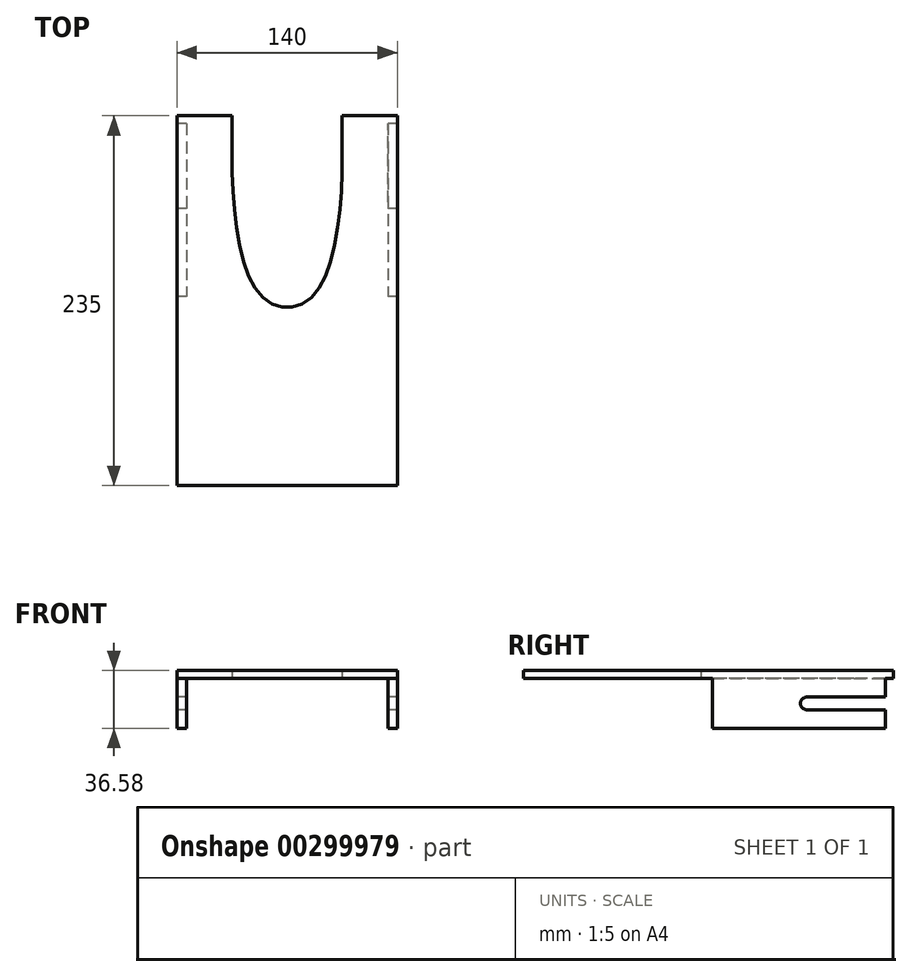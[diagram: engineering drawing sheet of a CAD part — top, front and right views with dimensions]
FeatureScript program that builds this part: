
annotation { "Feature Type Name" : "Feature", "Feature Type Description" : "" }
export const myFeature = defineFeature(function(context is Context, id is Id, definition is map)
    precondition{}
    {
        {
            var Q0;
            Q0=qCreatedBy(makeId("Top.planeOp"),FACE);
            var sketch = newSketch(context, id + "F0", { "sketchPlane" : qUnion([Q0])});
            skLineSegment(sketch, "E0.bottom", {"start": v(-66.5, 0) * mm, "end": v(73.5, 0) * mm});
            skLineSegment(sketch, "E0.top", {"start": v(-66.5, 110) * mm, "end": v(73.5, 110) * mm});
            skLineSegment(sketch, "E0.left", {"start": v(-66.5, 0) * mm, "end": v(-66.5, 110) * mm});
            skLineSegment(sketch, "E0.right", {"start": v(73.5, 0) * mm, "end": v(73.5, 110) * mm});
            skLineSegment(sketch, "E1", {"start": v(-66.5, 110) * mm, "end": v(-66.5, 210) * mm});
            skLineSegment(sketch, "E2", {"start": v(-66.5, 210) * mm, "end": v(-31.5, 210) * mm});
            skLineSegment(sketch, "E3", {"start": v(73.5, 110) * mm, "end": v(73.5, 210) * mm});
            skLineSegment(sketch, "E4", {"start": v(73.5, 210) * mm, "end": v(38.5, 210) * mm});
            skFitSpline(sketch, "E5", {"points": [v(-31.5, 210) * mm, v(-12.5, 120) * mm, v(19.5, 120) * mm, v(38.5, 210) * mm], "startDerivative": vector(0, -248.62) * mm, "endDerivative": vector(0, 248.62) * mm});
            skLineSegment(sketch, "E6.top", {"start": v(-66.5, 235) * mm, "end": v(-31.5, 235) * mm});
            skLineSegment(sketch, "E6.left", {"start": v(-66.5, 210) * mm, "end": v(-66.5, 235) * mm});
            skLineSegment(sketch, "E6.right", {"start": v(-31.5, 210) * mm, "end": v(-31.5, 235) * mm});
            skLineSegment(sketch, "E7.top", {"start": v(73.5, 235) * mm, "end": v(38.5, 235) * mm});
            skLineSegment(sketch, "E7.left", {"start": v(73.5, 210) * mm, "end": v(73.5, 235) * mm});
            skLineSegment(sketch, "E7.right", {"start": v(38.5, 210) * mm, "end": v(38.5, 235) * mm});
            skSolve(sketch);
        }
        {
            var Q0;
            Q0=qSketchRegion(id+"F0",true);
            extrude(context, id + "F1", {"entities" : qUnion([Q0]), "depth" : 4.83 * mm, "offsetDistance" : 25 * mm});
        }
        {
            var Q0;
            Q0=makeQuery(id+"F1.opExtrude","SWEPT_FACE",FACE,{"disambiguationData":[OSD([sQuery(id+"F0.wireOp",EDGE,"E0.bottom")])]});
            var sketch = newSketch(context, id + "F2", { "sketchPlane" : qUnion([Q0])});
            skLineSegment(sketch, "E8.bottom", {"start": v(-66.5, 0) * mm, "end": v(-34.75, 0) * mm});
            skLineSegment(sketch, "E8.top", {"start": v(-66.5, -31.75) * mm, "end": v(-34.75, -31.75) * mm});
            skLineSegment(sketch, "E8.left", {"start": v(-66.5, 0) * mm, "end": v(-66.5, -31.75) * mm});
            skLineSegment(sketch, "E8.right", {"start": v(-34.75, 0) * mm, "end": v(-34.75, -31.75) * mm});
            skLineSegment(sketch, "E9.bottom", {"start": v(73.5, 0) * mm, "end": v(41.75, 0) * mm});
            skLineSegment(sketch, "E9.top", {"start": v(73.5, -31.75) * mm, "end": v(41.75, -31.75) * mm});
            skLineSegment(sketch, "E9.left", {"start": v(73.5, 0) * mm, "end": v(73.5, -31.75) * mm});
            skLineSegment(sketch, "E9.right", {"start": v(41.75, 0) * mm, "end": v(41.75, -31.75) * mm});
            skLineSegment(sketch, "E10.bottom", {"start": v(-63.33, -3.17) * mm, "end": v(-37.93, -3.17) * mm});
            skLineSegment(sketch, "E10.top", {"start": v(-63.33, -28.57) * mm, "end": v(-37.93, -28.57) * mm});
            skLineSegment(sketch, "E10.left", {"start": v(-63.33, -3.17) * mm, "end": v(-63.33, -28.57) * mm});
            skLineSegment(sketch, "E10.right", {"start": v(-37.93, -3.17) * mm, "end": v(-37.93, -28.57) * mm});
            skLineSegment(sketch, "E11.bottom", {"start": v(44.92, -3.18) * mm, "end": v(70.33, -3.17) * mm});
            skLineSegment(sketch, "E11.top", {"start": v(44.92, -28.58) * mm, "end": v(70.33, -28.58) * mm});
            skLineSegment(sketch, "E11.left", {"start": v(44.92, -3.18) * mm, "end": v(44.92, -28.58) * mm});
            skLineSegment(sketch, "E11.right", {"start": v(70.33, -3.17) * mm, "end": v(70.33, -28.58) * mm});
            skSolve(sketch);
        }
        {
            var Q0;
            Q0=qSketchRegion(id+"F2",true);
            extrude(context, id + "F3", {"entities" : qUnion([Q0]), "operationType" : NewBodyOperationType.ADD, "oppositeDirection" : true, "depth" : 120 * mm});
        }
        {
            var Q0;
            Q0=makeQuery(id+"F3.opExtrude","CAP_FACE",FACE,{"disambiguationData":[OSD([sQuery(id+"F2.wireOp",EDGE,"E9.bottom"),sQuery(id+"F2.wireOp",EDGE,"E9.top"),sQuery(id+"F2.wireOp",EDGE,"E9.left"),sQuery(id+"F2.wireOp",EDGE,"E9.right"),sQuery(id+"F2.wireOp",EDGE,"E11.bottom"),sQuery(id+"F2.wireOp",EDGE,"E11.top"),sQuery(id+"F2.wireOp",EDGE,"E11.left"),sQuery(id+"F2.wireOp",EDGE,"E11.right")])],"isStart":false});
            var sketch = newSketch(context, id + "F4", { "sketchPlane" : qUnion([Q0])});
            skPoint(sketch, "E12.oppositeSnap0", {"position": v(-70.33, -15.88) * mm});
            skLineSegment(sketch, "E12.bottom", {"start": v(-73.5, 0) * mm, "end": v(-56, 0) * mm});
            skLineSegment(sketch, "E12.top", {"start": v(-73.5, -31.75) * mm, "end": v(-70.33, -31.75) * mm});
            skLineSegment(sketch, "E12.left", {"start": v(-73.5, 0) * mm, "end": v(-73.5, -31.75) * mm});
            skLineSegment(sketch, "E13.bottom", {"start": v(56, -31.75) * mm, "end": v(66.5, -31.75) * mm});
            skLineSegment(sketch, "E13.top", {"start": v(56, 0) * mm, "end": v(66.5, 0) * mm});
            skLineSegment(sketch, "E13.right", {"start": v(66.5, -31.75) * mm, "end": v(66.5, 0) * mm});
            skLineSegment(sketch, "E14", {"start": v(60.5, -31.75) * mm, "end": v(60.5, 0) * mm});
            skLineSegment(sketch, "E15", {"start": v(-67.5, 0) * mm, "end": v(-67.5, -31.75) * mm});
            skSolve(sketch);
        }
        {
            var Q0;
            Q0=qSketchRegion(id+"F4",true);
            var Q1;
            {var subQ5=makeQuery(id+"F3.opExtrude","CAP_EDGE",EDGE,{"disambiguationData":[OSD([sQuery(id+"F2.wireOp",EDGE,"E11.right")])],"isStart":false});Q1=makeQuery(id+"F4.imprint","IMPRINT",FACE,{"disambiguationData":[TD([[makeQuery(id+"F4.imprint","IMPRINT",EDGE,{"derivedFrom":subQ5}),1.0]])]});}
            var Q2;
            {var subQ6=sQuery(id+"F4.wireOp",EDGE,"E12.top");Q2=makeQuery(id+"F4.imprint","IMPRINT",FACE,{"disambiguationData":[TD([[makeQuery(id+"F4.imprint","IMPRINT",EDGE,{"derivedFrom":subQ6}),1.0]])]});}
            extrude(context, id + "F5", {"entities" : qUnion([Q0, Q1, Q2]), "operationType" : NewBodyOperationType.ADD, "depth" : 110 * mm, "offsetDistance" : 25 * mm});
        }
        {
            var Q0;
            {var subQ0=sQuery(id+"F2.wireOp",EDGE,"E8.right");Q0=makeQuery(id+"FrnK0tPHe9QpJH6_1.boolean.opBoolean","MERGE",FACE,{"derivedFrom":[makeQuery(id+"F3.opExtrude","SWEPT_FACE",FACE,{"disambiguationData":[OSD([subQ0])]}),makeQuery(id+"FrnK0tPHe9QpJH6_1.opExtrude","SWEPT_FACE",FACE,{"disambiguationData":[OSD([subQ0])]})]});}
            var sketch = newSketch(context, id + "F6", { "sketchPlane" : qUnion([Q0])});
            skCircle(sketch, "E16", {"center": v(60, -10) * mm, "radius": 3 * mm});
            skSolve(sketch);
        }
        {
            var Q0;
            Q0=qSketchRegion(id+"F6",true);
            extrude(context, id + "F7", {"entities" : qUnion([Q0]), "operationType" : NewBodyOperationType.REMOVE, "oppositeDirection" : true, "depth" : 10 * mm});
        }
        {
            var Q0;
            Q0=makeQuery(id+"F3.boolean.opBoolean","MERGE",FACE,{"derivedFrom":[makeQuery(id+"F1.opExtrude","SWEPT_FACE",FACE,{"disambiguationData":[OSD([sQuery(id+"F0.wireOp",EDGE,"E0.bottom")])]}),makeQuery(id+"F3.opExtrude","CAP_FACE",FACE,{"disambiguationData":[OSD([sQuery(id+"F2.wireOp",EDGE,"E8.bottom"),sQuery(id+"F2.wireOp",EDGE,"E8.top"),sQuery(id+"F2.wireOp",EDGE,"E8.left"),sQuery(id+"F2.wireOp",EDGE,"E8.right"),sQuery(id+"F2.wireOp",EDGE,"E10.bottom"),sQuery(id+"F2.wireOp",EDGE,"E10.top"),sQuery(id+"F2.wireOp",EDGE,"E10.left"),sQuery(id+"F2.wireOp",EDGE,"E10.right")])],"isStart":true}),makeQuery(id+"F3.opExtrude","CAP_FACE",FACE,{"disambiguationData":[OSD([sQuery(id+"F2.wireOp",EDGE,"E9.bottom"),sQuery(id+"F2.wireOp",EDGE,"E9.top"),sQuery(id+"F2.wireOp",EDGE,"E9.left"),sQuery(id+"F2.wireOp",EDGE,"E9.right"),sQuery(id+"F2.wireOp",EDGE,"E11.bottom"),sQuery(id+"F2.wireOp",EDGE,"E11.top"),sQuery(id+"F2.wireOp",EDGE,"E11.left"),sQuery(id+"F2.wireOp",EDGE,"E11.right")])],"isStart":true})]});
            var sketch = newSketch(context, id + "F8", { "sketchPlane" : qUnion([Q0])});
            skLineSegment(sketch, "E17.bottom", {"start": v(-63.33, -3.17) * mm, "end": v(-37.93, -3.17) * mm});
            skLineSegment(sketch, "E17.top", {"start": v(-63.33, -28.57) * mm, "end": v(-37.93, -28.57) * mm});
            skLineSegment(sketch, "E17.left", {"start": v(-63.33, -3.18) * mm, "end": v(-63.33, -28.57) * mm});
            skLineSegment(sketch, "E17.right", {"start": v(-37.93, -3.18) * mm, "end": v(-37.93, -28.57) * mm});
            skLineSegment(sketch, "E18.bottom", {"start": v(-58.56, -7.94) * mm, "end": v(-42.69, -7.94) * mm});
            skLineSegment(sketch, "E18.top", {"start": v(-58.56, -23.81) * mm, "end": v(-42.69, -23.81) * mm});
            skLineSegment(sketch, "E18.left", {"start": v(-58.56, -7.94) * mm, "end": v(-58.56, -23.81) * mm});
            skLineSegment(sketch, "E18.right", {"start": v(-42.69, -7.94) * mm, "end": v(-42.69, -23.81) * mm});
            skLineSegment(sketch, "E19.bottom", {"start": v(44.92, -3.18) * mm, "end": v(70.33, -3.18) * mm});
            skLineSegment(sketch, "E19.top", {"start": v(44.92, -28.58) * mm, "end": v(70.33, -28.58) * mm});
            skLineSegment(sketch, "E19.left", {"start": v(44.92, -3.18) * mm, "end": v(44.92, -28.58) * mm});
            skLineSegment(sketch, "E19.right", {"start": v(70.33, -3.18) * mm, "end": v(70.33, -28.58) * mm});
            skLineSegment(sketch, "E20.bottom", {"start": v(49.69, -7.94) * mm, "end": v(65.56, -7.94) * mm});
            skLineSegment(sketch, "E20.top", {"start": v(49.69, -23.81) * mm, "end": v(65.56, -23.81) * mm});
            skLineSegment(sketch, "E20.left", {"start": v(49.69, -7.94) * mm, "end": v(49.69, -23.81) * mm});
            skLineSegment(sketch, "E20.right", {"start": v(65.56, -7.94) * mm, "end": v(65.56, -23.81) * mm});
            skSolve(sketch);
        }
        {
            var Q0;
            Q0=qSketchRegion(id+"F8",true);
            extrude(context, id + "F9", {"entities" : qUnion([Q0]), "operationType" : NewBodyOperationType.ADD, "endBound" : BoundingType.SYMMETRIC, "depth" : 40 * mm, "offsetDistance" : 25 * mm});
        }
        {
            var Q0;
            Q0=makeQuery(id+"F5.boolean.opBoolean","MERGE",FACE,{"derivedFrom":[makeQuery(id+"F3.opExtrude","SWEPT_FACE",FACE,{"disambiguationData":[OSD([sQuery(id+"F2.wireOp",EDGE,"E8.left")])]}),makeQuery(id+"F5.opExtrude","SWEPT_FACE",FACE,{"disambiguationData":[OSD([sQuery(id+"F4.wireOp",EDGE,"E13.right")])]})]});
            var sketch = newSketch(context, id + "F10", { "sketchPlane" : qUnion([Q0])});
            skCircle(sketch, "E21", {"center": v(-180, -16) * mm, "radius": 4 * mm});
            skLineSegment(sketch, "E22", {"start": v(-180, -16) * mm, "end": v(-180, -12) * mm});
            skLineSegment(sketch, "E23", {"start": v(-180, -12) * mm, "end": v(-230, -12) * mm});
            skLineSegment(sketch, "E24", {"start": v(-180, -16) * mm, "end": v(-180, -20) * mm});
            skLineSegment(sketch, "E25", {"start": v(-180, -20) * mm, "end": v(-230, -20) * mm});
            skSolve(sketch);
        }
        {
            var Q0;
            Q0=qSketchRegion(id+"F10",true);
            var Q1;
            {var subQ0=sQuery(id+"F10.wireOp",EDGE,"E23");Q1=makeQuery(id+"F10.imprint","IMPRINT",FACE,{"disambiguationData":[TD([[makeQuery(id+"F10.imprint","IMPRINT",EDGE,{"derivedFrom":subQ0}),1.0]])]});}
            extrude(context, id + "F11", {"entities" : qUnion([Q0, Q1]), "operationType" : NewBodyOperationType.REMOVE, "oppositeDirection" : true, "depth" : 152 * mm, "offsetDistance" : 25 * mm});
        }
        {
            var Q0;
            Q0=makeQuery(id+"F5.boolean.opBoolean","MERGE",FACE,{"derivedFrom":[makeQuery(id+"F3.opExtrude","SWEPT_FACE",FACE,{"disambiguationData":[OSD([sQuery(id+"F2.wireOp",EDGE,"E8.left")])]}),makeQuery(id+"F5.opExtrude","SWEPT_FACE",FACE,{"disambiguationData":[OSD([sQuery(id+"F4.wireOp",EDGE,"E13.right")])]})]});
            var sketch = newSketch(context, id + "F12", { "sketchPlane" : qUnion([Q0])});
            skLineSegment(sketch, "E26.bottom", {"start": v(-236.3, 0) * mm, "end": v(11.4, 0) * mm});
            skLineSegment(sketch, "E26.top", {"start": v(-236.3, 41.8) * mm, "end": v(11.4, 41.8) * mm});
            skLineSegment(sketch, "E26.left", {"start": v(-236.3, 0) * mm, "end": v(-236.3, 41.8) * mm});
            skLineSegment(sketch, "E26.right", {"start": v(11.4, 0) * mm, "end": v(11.4, 41.8) * mm});
            skLineSegment(sketch, "E27.bottom", {"start": v(-120, 64.16) * mm, "end": v(43.4, 64.16) * mm});
            skLineSegment(sketch, "E27.top", {"start": v(-120, -61.88) * mm, "end": v(43.4, -61.88) * mm});
            skLineSegment(sketch, "E27.left", {"start": v(-120, 64.16) * mm, "end": v(-120, -61.88) * mm});
            skLineSegment(sketch, "E27.right", {"start": v(43.4, 64.16) * mm, "end": v(43.4, -61.88) * mm});
            skSolve(sketch);
        }
        {
            var Q0;
            {var subQ6=sQuery(id+"F12.wireOp",EDGE,"E26.left");Q0=makeQuery(id+"F12.imprint","IMPRINT",FACE,{"disambiguationData":[TD([[makeQuery(id+"F12.imprint","IMPRINT",EDGE,{"derivedFrom":subQ6}),-1.0]])]});}
            var Q1;
            {var subQ1=sQuery(id+"F12.wireOp",EDGE,"E26.right");Q1=makeQuery(id+"F12.imprint","IMPRINT",FACE,{"disambiguationData":[TD([[makeQuery(id+"F12.imprint","IMPRINT",EDGE,{"derivedFrom":subQ1}),-1.0]])]});}
            var Q2;
            {var subQ0=sQuery(id+"F12.wireOp",EDGE,"E27.left");var subQ1=sQuery(id+"F12.wireOp",EDGE,"E26.bottom");var subQ2=makeQuery(id+"F12.imprint","INTERSECT",VERTEX,{"derivedFrom":[subQ1,subQ0]});var subQ3=sQuery(id+"F2.wireOp",EDGE,"E8.left");var subQ4=makeQuery(id+"F3.boolean.opBoolean","MERGE",EDGE,{"derivedFrom":[makeQuery(id+"F1.opExtrude","SWEPT_EDGE",EDGE,{"disambiguationData":[OSD([sQuery(id+"F0.wireOp",EDGE,"E0.bottom"),sQuery(id+"F0.wireOp",EDGE,"E0.left")])]}),makeQuery(id+"F3.opExtrude","CAP_EDGE",EDGE,{"disambiguationData":[OSD([subQ3])],"isStart":true})]});var subQ5=makeQuery(id+"F12.imprint","INTERSECT",VERTEX,{"derivedFrom":[subQ4,subQ1]});Q2=makeQuery(id+"F12.imprint","IMPRINT",FACE,{"disambiguationData":[TD([[makeQuery(id+"F12.imprint","IMPRINT",EDGE,{"disambiguationData":[TD([[subQ2,-1.0],[subQ5,1.0]])],"derivedFrom":subQ1}),-1.0]])]});}
            var Q3;
            {var subQ8=sQuery(id+"F12.wireOp",EDGE,"E26.right");Q3=makeQuery(id+"F12.imprint","IMPRINT",FACE,{"disambiguationData":[TD([[makeQuery(id+"F12.imprint","IMPRINT",EDGE,{"derivedFrom":subQ8}),1.0]])]});}
            var Q4;
            Q4=makeQuery(id+"F12.imprint","IMPRINT",FACE,{"disambiguationData":[TD([[makeQuery(id+"F12.imprint","IMPRINT",EDGE,{"derivedFrom":makeQuery(id+"F11.boolean.opBoolean","COPY",EDGE,{"derivedFrom":makeQuery(id+"F11.opExtrude","CAP_EDGE",EDGE,{"disambiguationData":[OSD([sQuery(id+"F10.wireOp",EDGE,"E21")])],"isStart":true})})}),-1.0]])]});
            extrude(context, id + "F13", {"entities" : qUnion([Q0, Q1, Q2, Q3, Q4]), "operationType" : NewBodyOperationType.REMOVE, "endBound" : BoundingType.THROUGH_ALL, "oppositeDirection" : true, "depth" : 25 * mm, "offsetDistance" : 25 * mm});
        }
    });
